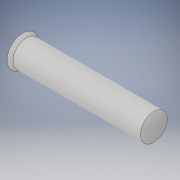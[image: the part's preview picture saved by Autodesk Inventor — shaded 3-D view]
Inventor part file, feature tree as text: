
AUTODESK INVENTOR PART (.ipt)
format: ipt  version: 2018.3 (Build 223284000, 284)  size: 101,888 bytes
history: native  units: in
note: dims shown in document units (in); Inventor stores cm internally (conversion verified against a paired STEP export)
features: revolve x1, sketch x1
ambient origin geometry x8: Origin, YZ Plane, XZ Plane, XY Plane, X Axis, Y Axis, Z Axis, Center Point
bodies: Solid1 (feature_tree)
feature tree (2):
  revolve  "Revolution1"  Angle=60.0deg
  sketch  "Sketch1"  dims[d0=0.091in d1=60.0deg d3=0.786in d4=0.0785in d5=0.32in d6=90.0deg]
